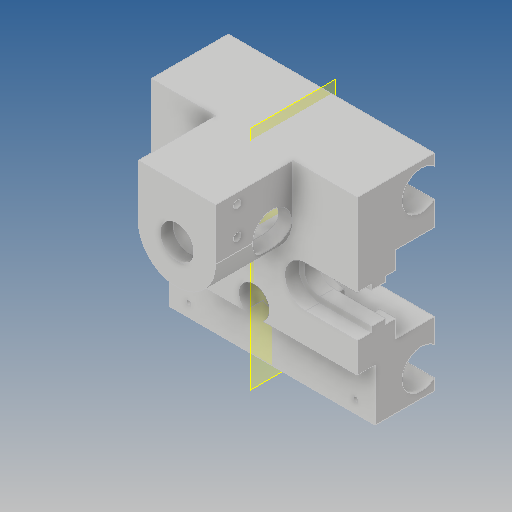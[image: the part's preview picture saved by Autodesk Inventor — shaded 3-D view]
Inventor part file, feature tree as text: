
AUTODESK INVENTOR PART (.ipt)
format: ipt  version: 2018 (Build 220112000, 112)  size: 360,448 bytes
history: native  units: mm
features: extrude x14, sketch x14, plane x2, mirror x2, other x1
ambient origin geometry x8: Origin, YZ Plane, XZ Plane, XY Plane, X Axis, Y Axis, Z Axis, Center Point
bodies: Solid1 (feature_tree)
feature tree (33):
  other  "<userpath>\OneDrive\Objet3D\3DPrinter\Parameters.xlsx"
  extrude  "Extrusion1"  Depth=80.0mm
  extrude  "Extrusion2"  Depth=40.0mm
  extrude  "Extrusion3"  Depth=12.2mm
  extrude  "Extrusion4"  Depth=10.0mm
  extrude  "Extrusion5"  Depth=5.5mm TaperAngle=0.0deg
  extrude  "Extrusion6"  Depth=4.0mm TaperAngle=0.0deg
  plane  "Work Plane1"
  mirror  "Mirror1"
  extrude  "Extrusion8"  Depth=8.1mm
  extrude  "Extrusion9"  Depth=25.0mm
  plane  "Work Plane2"
  mirror  "Mirror2"
  extrude  "Extrusion10"  Depth=15.0mm
  extrude  "Extrusion11"  Depth=5.0mm
  extrude  "Extrusion12"  Depth=5.0mm
  extrude  "Extrusion13"  Depth=0.0mm
  extrude  "Extrusion14"  Depth=15.0mm
  extrude  "Extrusion15"  Depth=10.0mm
  sketch  "Sketch1"  dims[d0=80.0mm d1=80.0mm]
  sketch  "Sketch2"  dims[d2=15.0mm d3=0.0mm d7=40.0mm]
  sketch  "Sketch3"  dims[d8=20.0mm d9=12.2mm]
  sketch  "Sketch4"  dims[d10=10.0mm d11=0.0mm d12=16.2mm]
  sketch  "Sketch5"  dims[d13=4.0mm d14=0.0mm d15=5.5mm d16=0.0mm]
  sketch  "Sketch6"  dims[d17=13.8mm d18=4.0mm d19=0.0mm]
  sketch  "Sketch8"  dims[d20=16.2mm d21=8.1mm]
  sketch  "Sketch9"  dims[d22=25.0mm d23=25.0mm]
  sketch  "Sketch10"  dims[d24=15.0mm d25=15.0mm]
  sketch  "Sketch11"  dims[d29=15.0mm d30=5.0mm d31=5.0mm d32=15.0mm]
  sketch  "Sketch12"  dims[d33=5.0mm d34=5.0mm]
  sketch  "Sketch13"  dims[d35=80.0mm d36=0.0mm d37=0.0mm]
  sketch  "Sketch14"  dims[d38=15.0mm d39=15.0mm]
  sketch  "Sketch15"  dims[d40=60.0mm d41=10.0mm d42=10.0mm d49=20.2mm d50=7.0mm d51=0.0mm d52=0.0mm d53=1.9mm d54=1.9mm d55=7.6mm d56=7.6mm d57=10.0mm d58=4.9mm d59=10.0mm d60=0.0mm d61=12.0mm d62=20.0mm d63=0.0mm d64=30.0mm d65=20.0mm d66=40.0mm d67=20.0mm d68=30.0mm d69=0.0mm d70=13.0mm d71=5.0mm d72=0.0mm d73=35.0mm d74=0.0mm d75=2.9mm d76=2.9mm d77=11.0mm d78=4.0mm d79=8.5mm d80=8.5mm d81=15.0mm d82=0.0mm d83=6.0mm d84=15.0mm d85=8.0mm d86=17.0mm d87=0.0mm]
